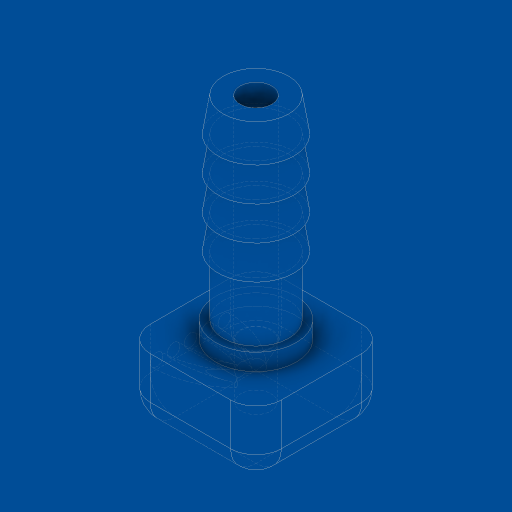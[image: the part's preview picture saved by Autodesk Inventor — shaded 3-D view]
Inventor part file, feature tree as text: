
AUTODESK INVENTOR PART (.ipt)
format: ipt  version: 2023.2 (Build 272271000, 271)  size: 256,000 bytes
history: native  units: mm
features: sketch x6, sweep x5, extrude x2, projected_geometry x2, revolve x1, hole x1, plane x1, fillet x1
ambient origin geometry x8: Origin, YZ Plane, XZ Plane, XY Plane, X Axis, Y Axis, Z Axis, Center Point
bodies: Solid1 (feature_tree)
feature tree (19):
  revolve  "Revolution1"  [1 undecoded]
  extrude  "Extrusion1"  Depth=2.0mm
  extrude  "Extrusion2"  TaperAngle=90.0deg  [1 undecoded]
  hole  "Hole1"  [1 undecoded]
  sketch  "Sketch8"  dims[d9=8.0mm d10=3.0mm]
  plane  "Work Plane1"
  sketch  "Sketch9"  dims[d11=15.525mm d12=15.525mm d13=0.0mm d14=3.571875mm d15=6.0mm d16=4.0mm d17=2.0mm d18=90.0deg d19=6.5mm d20=0.0mm d21=1.5mm d22=50.0mm d24=2.0mm d25=10.0mm d27=10.0mm d29=0.0mm d30=0.0mm d31=0.0mm d32=0.0mm d33=0.0mm d34=0.0mm d35=0.0mm d36=0.0mm d37=0.0mm d38=0.0mm d39=3.0mm]
  sweep  "Sweep1"
  sweep  "Sweep2"
  sweep  "Sweep3"
  sweep  "Sweep4"
  sweep  "Sweep5"
  fillet  "Fillet1"  [1 undecoded]
  sketch  "Sketch2"  dims[d0=23.0mm d1=7.75mm]
  sketch  "Sketch5"  dims[d2=9.0mm d3=2.0mm]
  sketch  "Sketch6"  dims[d4=4.0mm d5=90.0deg]
  sketch  "Sketch7"  dims[d6=9.525mm d7=2.0mm d8=0.0mm]
  projected_geometry  "Projected Loop1"
  projected_geometry  "Projected Loop2"
note: 4 required parameter values undecoded (feature->parameter linkage not recoverable at this tier; creation-order binding heuristic only, values carry confidence <= 0.55)